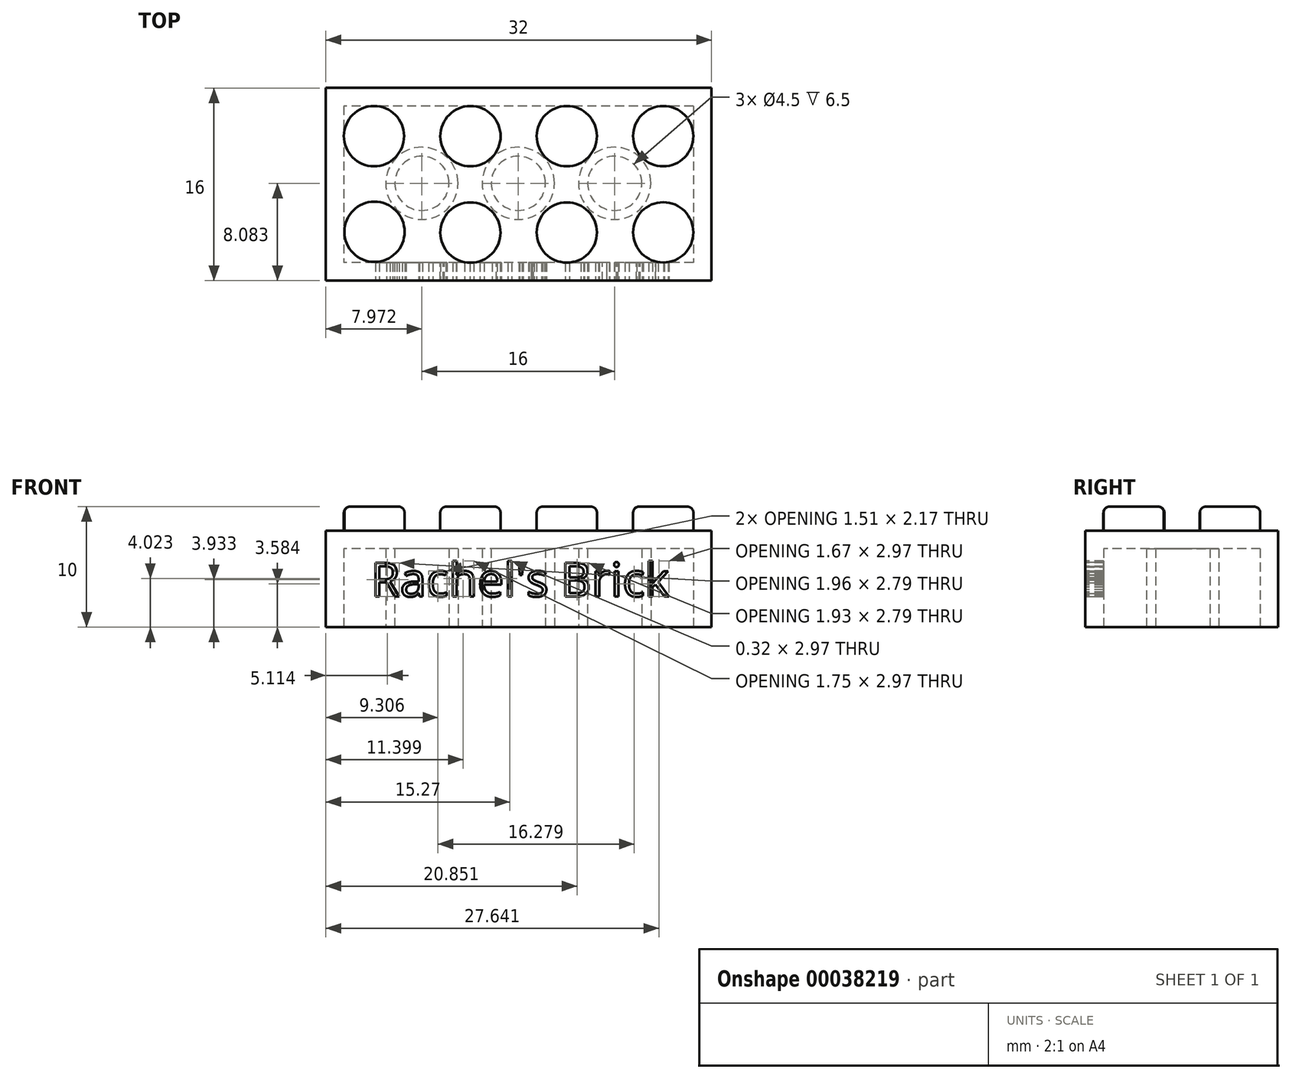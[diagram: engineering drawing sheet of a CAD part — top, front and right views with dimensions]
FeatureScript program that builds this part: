
annotation { "Feature Type Name" : "Feature", "Feature Type Description" : "" }
export const myFeature = defineFeature(function(context is Context, id is Id, definition is map)
    precondition{}
    {
        {
            var Q0;
            Q0=qCreatedBy(makeId("Top.planeOp"),FACE);
            var sketch = newSketch(context, id + "F0", { "sketchPlane" : qUnion([Q0])});
            skLineSegment(sketch, "E0.rect.bottom", {"start": v(-10.92, -30.3) * mm, "end": v(-42.92, -30.3) * mm});
            skLineSegment(sketch, "E0.rect.top", {"start": v(-10.92, -46.3) * mm, "end": v(-42.92, -46.3) * mm});
            skLineSegment(sketch, "E0.rect.left", {"start": v(-10.92, -30.3) * mm, "end": v(-10.92, -46.3) * mm});
            skLineSegment(sketch, "E0.rect.right", {"start": v(-42.92, -30.3) * mm, "end": v(-42.92, -46.3) * mm});
            skPoint(sketch, "E0.rect.middle", {"position": v(-26.92, -38.3) * mm});
            skSolve(sketch);
        }
        {
            var Q0;
            Q0=makeQuery(id+"F0.imprint","IMPRINT",FACE,{"disambiguationData":[TD([[makeQuery(id+"F0.imprint","IMPRINT",EDGE,{"derivedFrom":sQuery(id+"F0.wireOp",EDGE,"E0.rect.bottom")}),1.0]])]});
            extrude(context, id + "F1", {"entities" : qUnion([Q0]), "offsetDistance" : 25 * mm, "depth" : 8 * mm});
        }
        {
            var Q0;
            Q0=qCreatedBy(makeId("Top.planeOp"),FACE);
            cPlane(context, id + "F2", {"entities" : qUnion([Q0]), "cplaneType" : CPlaneType.OFFSET, "offset" : 8 * mm, "width" : 150 * mm, "height" : 150 * mm});
        }
        {
            var Q0;
            Q0=makeQuery(id+"F1.opExtrude","CAP_FACE",FACE,{"disambiguationData":[OSD([sQuery(id+"F0.wireOp",EDGE,"E0.rect.bottom"),sQuery(id+"F0.wireOp",EDGE,"E0.rect.top"),sQuery(id+"F0.wireOp",EDGE,"E0.rect.left"),sQuery(id+"F0.wireOp",EDGE,"E0.rect.right")])],"isStart":true});
            shell(context, id + "F3", {"entities" : qUnion([Q0]), "thickness" : 1.5 * mm});
        }
        {
            var Q0;
            Q0=makeQuery(id+"F1.opExtrude","CAP_FACE",FACE,{"disambiguationData":[OSD([sQuery(id+"F0.wireOp",EDGE,"E0.rect.bottom"),sQuery(id+"F0.wireOp",EDGE,"E0.rect.top"),sQuery(id+"F0.wireOp",EDGE,"E0.rect.left"),sQuery(id+"F0.wireOp",EDGE,"E0.rect.right")])],"isStart":false});
            var sketch = newSketch(context, id + "F4", { "sketchPlane" : qUnion([Q0])});
            skCircle(sketch, "E1", {"center": v(-38.92, -34.3) * mm, "radius": 2.5 * mm});
            skCircle(sketch, "E2", {"center": v(-14.92, -42.29) * mm, "radius": 2.5 * mm});
            skCircle(sketch, "E3", {"center": v(-22.92, -42.3) * mm, "radius": 2.5 * mm});
            skCircle(sketch, "E4", {"center": v(-30.91, -34.3) * mm, "radius": 2.5 * mm});
            skCircle(sketch, "E5", {"center": v(-22.92, -34.3) * mm, "radius": 2.5 * mm});
            skCircle(sketch, "E6", {"center": v(-14.92, -34.3) * mm, "radius": 2.5 * mm});
            skCircle(sketch, "E7", {"center": v(-30.92, -42.3) * mm, "radius": 2.5 * mm});
            skCircle(sketch, "E8", {"center": v(-38.88, -42.24) * mm, "radius": 2.5 * mm});
            skLineSegment(sketch, "E9", {"start": v(-42.96, -27.1) * mm, "end": v(-34.96, -27.1) * mm});
            skLineSegment(sketch, "E10", {"start": v(-34.96, -27.1) * mm, "end": v(-26.96, -27.1) * mm});
            skLineSegment(sketch, "E11", {"start": v(-26.96, -27.1) * mm, "end": v(-18.96, -27.1) * mm});
            skLineSegment(sketch, "E12", {"start": v(-18.96, -27.1) * mm, "end": v(-10.96, -27.1) * mm});
            skLineSegment(sketch, "E13", {"start": v(-42.92, -30.3) * mm, "end": v(-42.96, -27.1) * mm});
            skLineSegment(sketch, "E14", {"start": v(-10.92, -30.3) * mm, "end": v(-10.96, -27.1) * mm});
            skLineSegment(sketch, "E15", {"start": v(-34.96, -27.1) * mm, "end": v(-34.96, -49.44) * mm, "construction": true});
            skLineSegment(sketch, "E16", {"start": v(-26.96, -27.1) * mm, "end": v(-26.96, -49.66) * mm, "construction": true});
            skLineSegment(sketch, "E17", {"start": v(-18.96, -27.1) * mm, "end": v(-18.96, -49.44) * mm, "construction": true});
            skLineSegment(sketch, "E18", {"start": v(-42.92, -38.3) * mm, "end": v(-10.92, -38.3) * mm, "construction": true});
            skCircle(sketch, "E19", {"center": v(-34.96, -38.3) * mm, "radius": 3 * mm});
            skCircle(sketch, "E20", {"center": v(-26.96, -38.3) * mm, "radius": 3 * mm});
            skCircle(sketch, "E21", {"center": v(-18.96, -38.3) * mm, "radius": 3 * mm});
            skSolve(sketch);
        }
        {
            var Q0;
            Q0=makeQuery(id+"F4.imprint","IMPRINT",FACE,{"disambiguationData":[TD([[makeQuery(id+"F4.imprint","IMPRINT",EDGE,{"derivedFrom":sQuery(id+"F4.wireOp",EDGE,"E8")}),1.0]])]});
            var Q1;
            Q1=makeQuery(id+"F4.imprint","IMPRINT",FACE,{"disambiguationData":[TD([[makeQuery(id+"F4.imprint","IMPRINT",EDGE,{"derivedFrom":sQuery(id+"F4.wireOp",EDGE,"E7")}),1.0]])]});
            var Q2;
            Q2=makeQuery(id+"F4.imprint","IMPRINT",FACE,{"disambiguationData":[TD([[makeQuery(id+"F4.imprint","IMPRINT",EDGE,{"derivedFrom":sQuery(id+"F4.wireOp",EDGE,"E3")}),1.0]])]});
            var Q3;
            Q3=makeQuery(id+"F4.imprint","IMPRINT",FACE,{"disambiguationData":[TD([[makeQuery(id+"F4.imprint","IMPRINT",EDGE,{"derivedFrom":sQuery(id+"F4.wireOp",EDGE,"E2")}),1.0]])]});
            var Q4;
            Q4=makeQuery(id+"F4.imprint","IMPRINT",FACE,{"disambiguationData":[TD([[makeQuery(id+"F4.imprint","IMPRINT",EDGE,{"derivedFrom":sQuery(id+"F4.wireOp",EDGE,"E1")}),1.0]])]});
            var Q5;
            Q5=makeQuery(id+"F4.imprint","IMPRINT",FACE,{"disambiguationData":[TD([[makeQuery(id+"F4.imprint","IMPRINT",EDGE,{"derivedFrom":sQuery(id+"F4.wireOp",EDGE,"E4")}),1.0]])]});
            var Q6;
            Q6=makeQuery(id+"F4.imprint","IMPRINT",FACE,{"disambiguationData":[TD([[makeQuery(id+"F4.imprint","IMPRINT",EDGE,{"derivedFrom":sQuery(id+"F4.wireOp",EDGE,"E5")}),1.0]])]});
            var Q7;
            Q7=makeQuery(id+"F4.imprint","IMPRINT",FACE,{"disambiguationData":[TD([[makeQuery(id+"F4.imprint","IMPRINT",EDGE,{"derivedFrom":sQuery(id+"F4.wireOp",EDGE,"E6")}),1.0]])]});
            extrude(context, id + "F5", {"entities" : qUnion([Q0, Q1, Q2, Q3, Q4, Q5, Q6, Q7]), "operationType" : NewBodyOperationType.ADD, "depth" : 2 * mm});
        }
        {
            var Q0;
            Q0=makeQuery(id+"F5.opExtrude","CAP_FACE",FACE,{"disambiguationData":[OSD([sQuery(id+"F4.wireOp",EDGE,"E8")])],"isStart":false});
            var Q1;
            Q1=makeQuery(id+"F5.opExtrude","CAP_FACE",FACE,{"disambiguationData":[OSD([sQuery(id+"F4.wireOp",EDGE,"E1")])],"isStart":false});
            var Q2;
            Q2=makeQuery(id+"F5.opExtrude","CAP_FACE",FACE,{"disambiguationData":[OSD([sQuery(id+"F4.wireOp",EDGE,"E7")])],"isStart":false});
            var Q3;
            Q3=makeQuery(id+"F5.opExtrude","CAP_FACE",FACE,{"disambiguationData":[OSD([sQuery(id+"F4.wireOp",EDGE,"E4")])],"isStart":false});
            var Q4;
            Q4=makeQuery(id+"F5.opExtrude","CAP_FACE",FACE,{"disambiguationData":[OSD([sQuery(id+"F4.wireOp",EDGE,"E3")])],"isStart":false});
            var Q5;
            Q5=makeQuery(id+"F5.opExtrude","CAP_FACE",FACE,{"disambiguationData":[OSD([sQuery(id+"F4.wireOp",EDGE,"E5")])],"isStart":false});
            var Q6;
            Q6=makeQuery(id+"F5.opExtrude","CAP_FACE",FACE,{"disambiguationData":[OSD([sQuery(id+"F4.wireOp",EDGE,"E2")])],"isStart":false});
            var Q7;
            Q7=makeQuery(id+"F5.opExtrude","CAP_FACE",FACE,{"disambiguationData":[OSD([sQuery(id+"F4.wireOp",EDGE,"E6")])],"isStart":false});
            fillet(context, id + "F6", {"entities" : qUnion([Q0, Q1, Q2, Q3, Q4, Q5, Q6, Q7]), "radius" : 0.5 * mm, "tangentPropagation" : true, "defaultsChanged" : false, "vertexSettings" : [], "allowEdgeOverflow" : false});
        }
        {
            var Q0;
            Q0=qCreatedBy(makeId("Top.planeOp"),FACE);
            var sketch = newSketch(context, id + "F7", { "sketchPlane" : qUnion([Q0])});
            skCircle(sketch, "E22", {"center": v(-34.95, -38.22) * mm, "radius": 3 * mm});
            skCircle(sketch, "E23", {"center": v(-26.95, -38.22) * mm, "radius": 3 * mm});
            skCircle(sketch, "E24", {"center": v(-18.95, -38.22) * mm, "radius": 3 * mm});
            skCircle(sketch, "E25", {"center": v(-34.95, -38.22) * mm, "radius": 2.25 * mm});
            skCircle(sketch, "E26", {"center": v(-26.95, -38.22) * mm, "radius": 2.25 * mm});
            skCircle(sketch, "E27", {"center": v(-18.95, -38.22) * mm, "radius": 2.25 * mm});
            skSolve(sketch);
        }
        {
            var Q0;
            Q0 = qSketchRegion(id + "F7", true);
            extrude(context, id + "F8", {"entities" : qUnion([Q0]), "operationType" : NewBodyOperationType.ADD, "depth" : 7.8 * mm, "offsetDistance" : 25 * mm});
        }
        {
            var Q0;
            Q0=makeQuery(id+"F1.opExtrude","SWEPT_FACE",FACE,{"disambiguationData":[OSD([sQuery(id+"F0.wireOp",EDGE,"E0.rect.top")])]});
            var sketch = newSketch(context, id + "F9", { "sketchPlane" : qUnion([Q0])});
            skText(sketch, "E28", { "text": "Rachel\'s Brick", "fontName": "OpenSans-Regular.ttf"});
            const initialGuessF9  = {"E28": [-0.03917, 0.00254, 1, 0, 0.00281]};
            skSetInitialGuess(sketch, initialGuessF9);
            skSolve(sketch);
        }
        {
            var Q0;
            Q0 = qSketchRegion(id + "F9", true);
            extrude(context, id + "F10", {"entities" : qUnion([Q0]), "operationType" : NewBodyOperationType.REMOVE, "oppositeDirection" : true, "depth" : 2.25 * mm, "offsetDistance" : 25 * mm});
        }
    });
